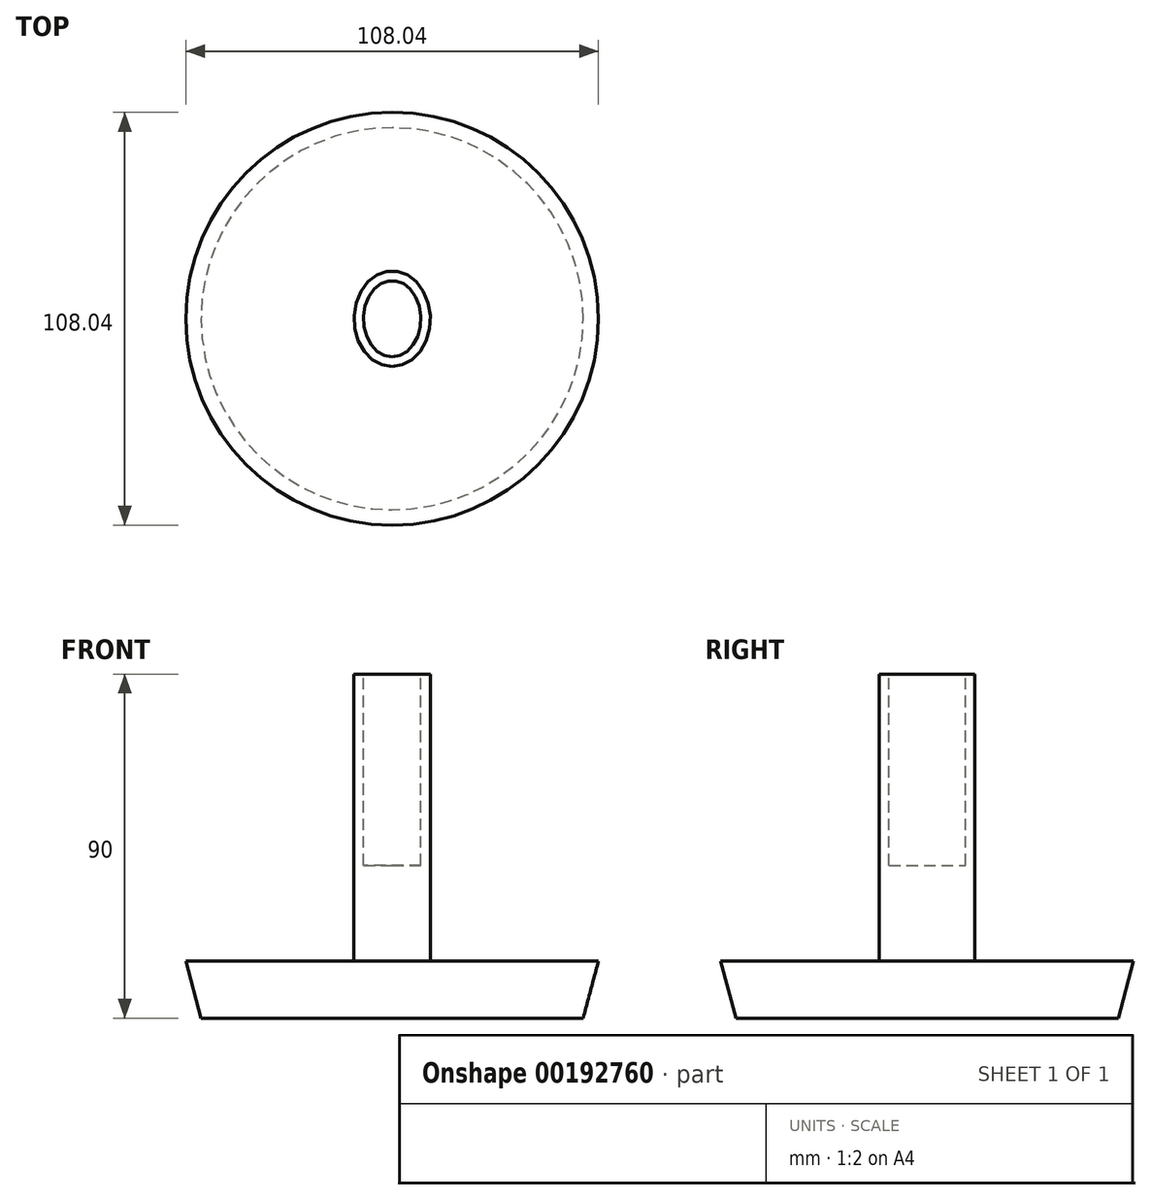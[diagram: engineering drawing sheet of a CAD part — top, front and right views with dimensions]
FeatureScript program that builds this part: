
annotation { "Feature Type Name" : "Feature", "Feature Type Description" : "" }
export const myFeature = defineFeature(function(context is Context, id is Id, definition is map)
    precondition{}
    {
        {
            var Q0;
            Q0=qCreatedBy(makeId("Top.planeOp"),FACE);
            var sketch = newSketch(context, id + "F0", { "sketchPlane" : qUnion([Q0])});
            skCircle(sketch, "E0", {"center": v(0, 0) * mm, "radius": 50 * mm});
            skSolve(sketch);
        }
        {
            var Q0;
            Q0 = qSketchRegion(id + "F0", true);
            extrude(context, id + "F1", {"entities" : qUnion([Q0]), "depth" : 15 * mm, "hasDraft" : true, "draftAngle" : 15 * degree});
        }
        {
            var Q0;
            Q0=makeQuery(id+"F1.opExtrude","CAP_FACE",FACE,{"disambiguationData":[OSD([sQuery(id+"F0.wireOp",EDGE,"E0")])],"isStart":false});
            var sketch = newSketch(context, id + "F2", { "sketchPlane" : qUnion([Q0])});
            skEllipse(sketch, "E1", {"center": v(0, 0) * mm, "majorRadius": 12.5 * mm, "minorRadius": 10 * mm, "majorAxis": v(0, -1)});
            skSolve(sketch);
        }
        {
            var Q0;
            Q0 = qSketchRegion(id + "F2", true);
            extrude(context, id + "F3", {"entities" : qUnion([Q0]), "operationType" : NewBodyOperationType.ADD, "depth" : 75 * mm});
        }
        {
            var Q0;
            Q0=makeQuery(id+"F3.opExtrude","CAP_FACE",FACE,{"disambiguationData":[OSD([sQuery(id+"F2.wireOp",EDGE,"E1")])],"isStart":false});
            var sketch = newSketch(context, id + "F4", { "sketchPlane" : qUnion([Q0])});
            skEllipse(sketch, "E2", {"center": v(0, 0) * mm, "majorRadius": 10 * mm, "minorRadius": 7.5 * mm, "majorAxis": v(0, -1)});
            skSolve(sketch);
        }
        {
            var Q0;
            Q0 = qSketchRegion(id + "F4", true);
            extrude(context, id + "F5", {"entities" : qUnion([Q0]), "operationType" : NewBodyOperationType.REMOVE, "oppositeDirection" : true, "depth" : 50 * mm});
        }
    });
